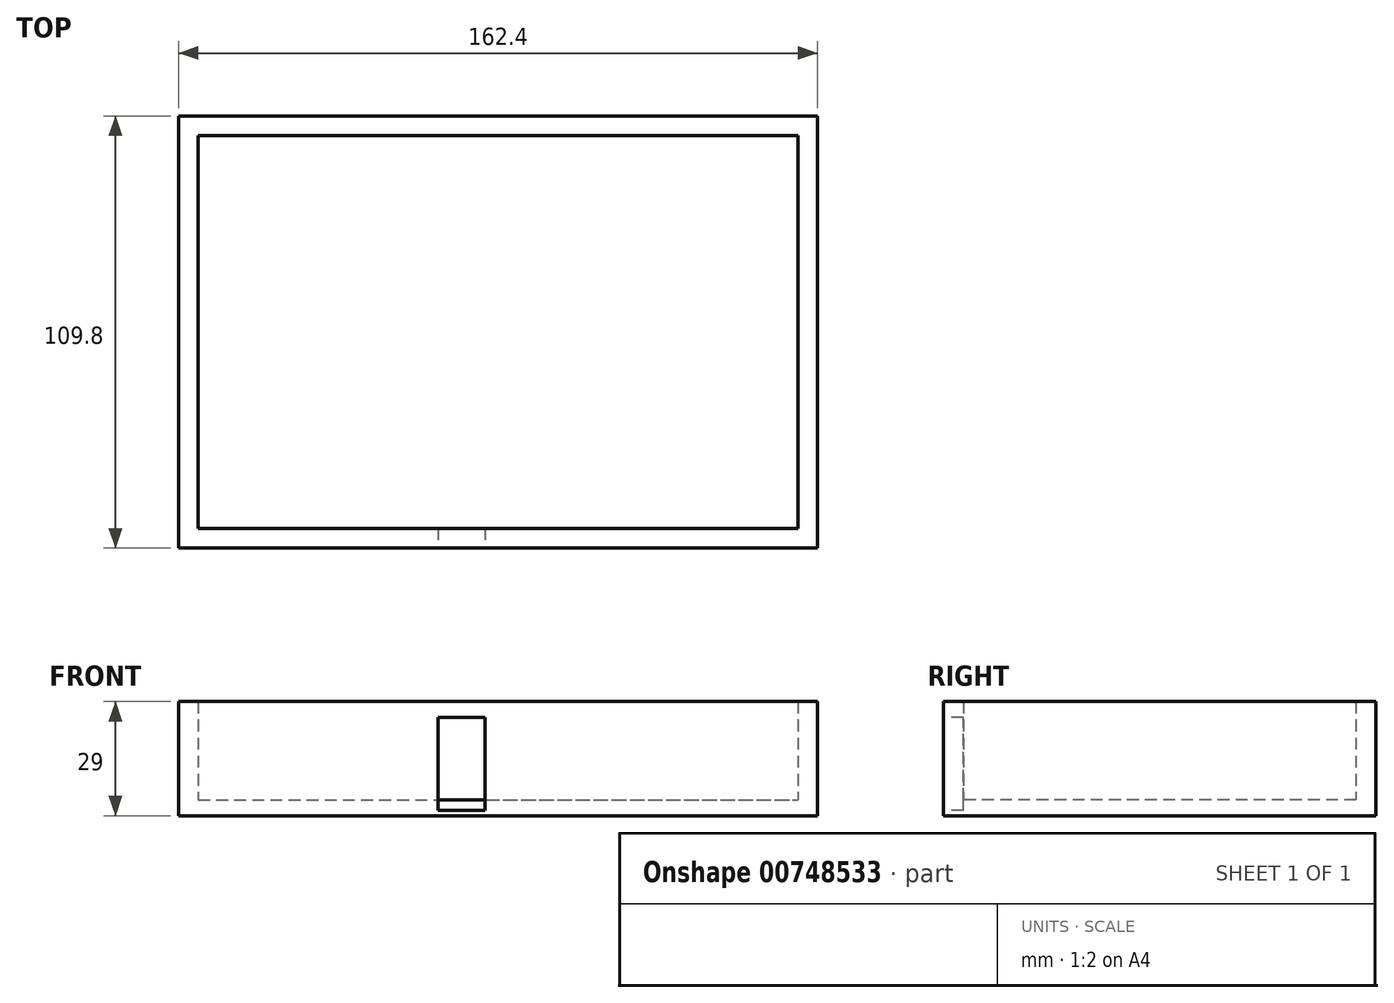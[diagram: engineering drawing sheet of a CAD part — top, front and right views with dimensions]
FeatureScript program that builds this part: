
annotation { "Feature Type Name" : "Feature", "Feature Type Description" : "" }
export const myFeature = defineFeature(function(context is Context, id is Id, definition is map)
    precondition{}
    {
        {
            var Q0;
            Q0=qCreatedBy(makeId("Top.planeOp"),FACE);
            var sketch = newSketch(context, id + "F0", { "sketchPlane" : qUnion([Q0])});
            skLineSegment(sketch, "E0.bottom", {"start": v(-79.79, 10.88) * mm, "end": v(82.61, 10.88) * mm});
            skLineSegment(sketch, "E0.top", {"start": v(-79.79, -98.92) * mm, "end": v(82.61, -98.92) * mm});
            skLineSegment(sketch, "E0.left", {"start": v(-79.79, 10.88) * mm, "end": v(-79.79, -98.92) * mm});
            skLineSegment(sketch, "E0.right", {"start": v(82.61, 10.88) * mm, "end": v(82.61, -98.92) * mm});
            skSolve(sketch);
        }
        {
            var Q0;
            Q0=makeQuery(id+"F0.imprint","IMPRINT",FACE,{"disambiguationData":[TD([[makeQuery(id+"F0.imprint","IMPRINT",EDGE,{"derivedFrom":sQuery(id+"F0.wireOp",EDGE,"E0.bottom")}),-1.0]])]});
            extrude(context, id + "F1", {"entities" : qUnion([Q0]), "depth" : 4 * mm, "offsetDistance" : 25 * mm});
        }
        {
            var Q0;
            Q0=makeQuery(id+"F1.opExtrude","CAP_FACE",FACE,{"disambiguationData":[OSD([sQuery(id+"F0.wireOp",EDGE,"E0.bottom"),sQuery(id+"F0.wireOp",EDGE,"E0.top"),sQuery(id+"F0.wireOp",EDGE,"E0.left"),sQuery(id+"F0.wireOp",EDGE,"E0.right")])],"isStart":false});
            var sketch = newSketch(context, id + "F2", { "sketchPlane" : qUnion([Q0])});
            skLineSegment(sketch, "E1.0", {"start": v(-74.79, 5.88) * mm, "end": v(-74.79, -93.92) * mm});
            skLineSegment(sketch, "E1.1", {"start": v(-74.79, 5.88) * mm, "end": v(77.61, 5.88) * mm});
            skLineSegment(sketch, "E1.2", {"start": v(77.61, 5.88) * mm, "end": v(77.61, -93.92) * mm});
            skLineSegment(sketch, "E1.3", {"start": v(-74.79, -93.92) * mm, "end": v(77.61, -93.92) * mm});
            skSolve(sketch);
        }
        {
            var Q0;
            Q0=makeQuery(id+"F2.imprint","IMPRINT",FACE,{"disambiguationData":[TD([[makeQuery(id+"F2.imprint","IMPRINT",EDGE,{"derivedFrom":sQuery(id+"F2.wireOp",EDGE,"E1.0")}),-1.0]])]});
            extrude(context, id + "F3", {"entities" : qUnion([Q0]), "operationType" : NewBodyOperationType.ADD, "depth" : 25 * mm, "offsetDistance" : 25 * mm});
        }
        {
            var Q0;
            {var subQ0=sQuery(id+"F0.wireOp",EDGE,"E0.top");Q0=makeQuery(id+"F3.boolean.opBoolean","MERGE",FACE,{"derivedFrom":[makeQuery(id+"F1.opExtrude","SWEPT_FACE",FACE,{"disambiguationData":[OSD([subQ0])]}),makeQuery(id+"F3.opExtrude","SWEPT_FACE",FACE,{"disambiguationData":[OSD([subQ0])]})]});}
            var sketch = newSketch(context, id + "F4", { "sketchPlane" : qUnion([Q0])});
            skLineSegment(sketch, "E2.left", {"start": v(-45.55, 19.69) * mm, "end": v(-45.55, 16.26) * mm});
            skLineSegment(sketch, "E2.right", {"start": v(-4.99, 19.69) * mm, "end": v(-4.99, 16.26) * mm});
            skLineSegment(sketch, "E3.bottom", {"start": v(-13.82, 1.3) * mm, "end": v(-1.92, 1.3) * mm});
            skLineSegment(sketch, "E3.top", {"start": v(-13.82, 24.91) * mm, "end": v(-1.92, 24.91) * mm});
            skLineSegment(sketch, "E3.left", {"start": v(-13.82, 1.3) * mm, "end": v(-13.82, 24.91) * mm});
            skLineSegment(sketch, "E3.right", {"start": v(-1.92, 1.3) * mm, "end": v(-1.92, 24.91) * mm});
            skSolve(sketch);
        }
        {
            var Q0;
            Q0=makeQuery(id+"F4.imprint","IMPRINT",FACE,{"disambiguationData":[TD([[makeQuery(id+"F4.imprint","IMPRINT",EDGE,{"derivedFrom":sQuery(id+"F4.wireOp",EDGE,"E3.bottom")}),1.0]])]});
            var sketch = newSketch(context, id + "F5", { "sketchPlane" : qUnion([Q0])});
            skSolve(sketch);
        }
        {
            var Q0;
            Q0=makeQuery(id+"F5.imprint","IMPRINT",FACE,{"disambiguationData":[TD([[makeQuery(id+"F5.imprint","IMPRINT",EDGE,{"derivedFrom":makeQuery(id+"F4.imprint","IMPRINT",EDGE,{"derivedFrom":sQuery(id+"F4.wireOp",EDGE,"E3.bottom")})}),1.0]])]});
            extrude(context, id + "F6", {"entities" : qUnion([Q0]), "operationType" : NewBodyOperationType.REMOVE, "oppositeDirection" : true, "depth" : 4 * mm, "offsetDistance" : 25 * mm});
        }
        {
            var Q0;
            Q0=makeQuery(id+"F4.imprint","IMPRINT",FACE,{"disambiguationData":[TD([[makeQuery(id+"F4.imprint","IMPRINT",EDGE,{"derivedFrom":sQuery(id+"F4.wireOp",EDGE,"E3.bottom")}),1.0]])]});
            extrude(context, id + "F7", {"entities" : qUnion([Q0]), "operationType" : NewBodyOperationType.REMOVE, "oppositeDirection" : true, "depth" : 5 * mm, "offsetDistance" : 25 * mm});
        }
    });
